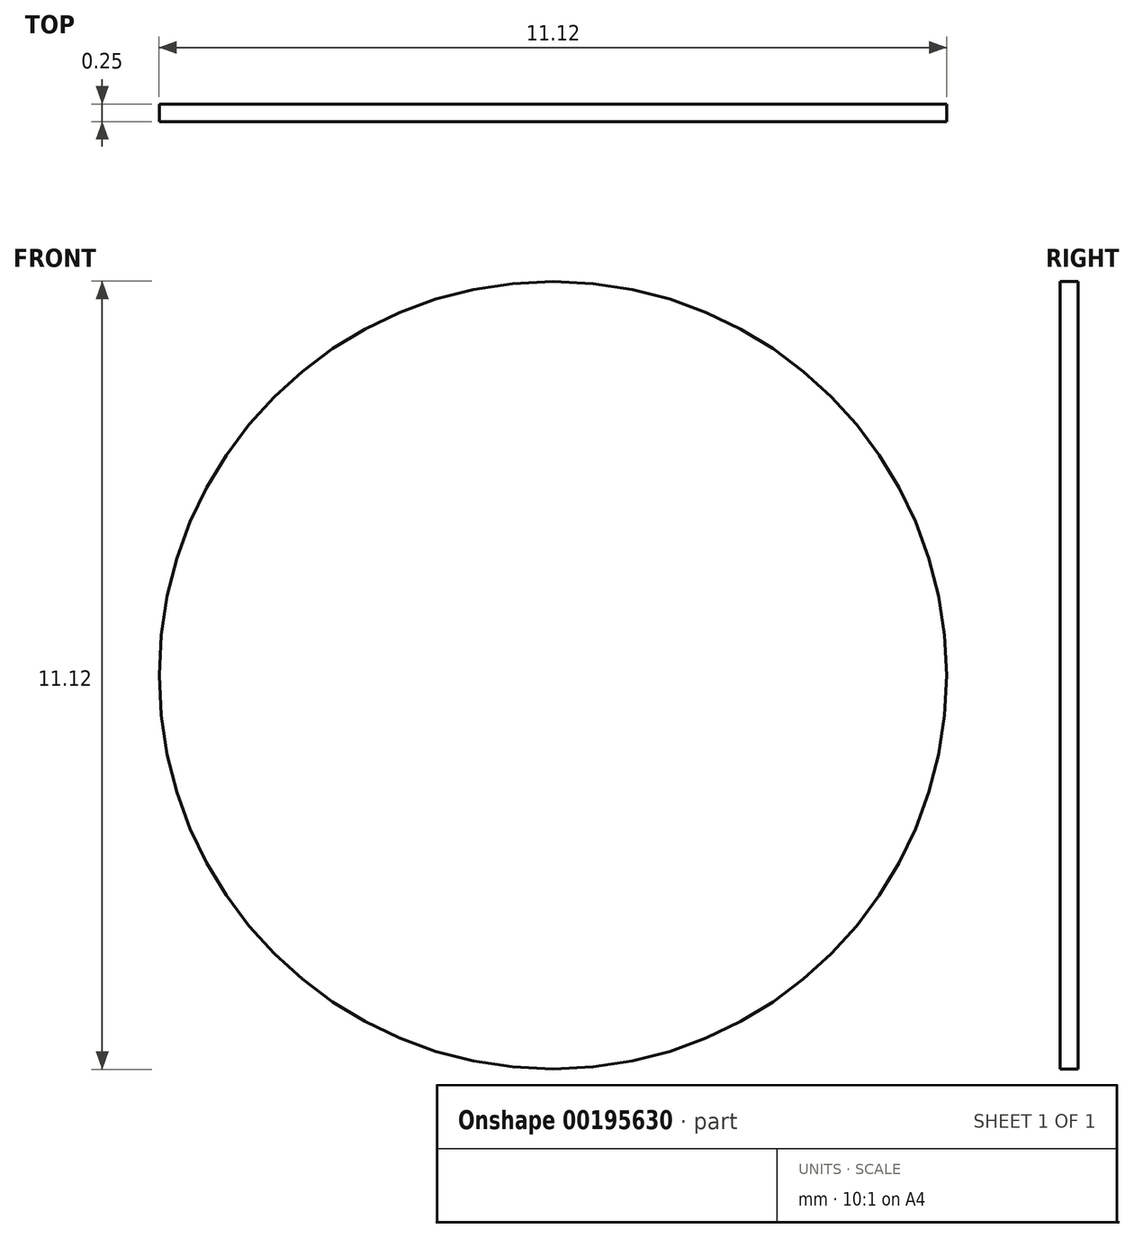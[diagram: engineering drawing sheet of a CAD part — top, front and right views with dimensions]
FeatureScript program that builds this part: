
annotation { "Feature Type Name" : "Feature", "Feature Type Description" : "" }
export const myFeature = defineFeature(function(context is Context, id is Id, definition is map)
    precondition{}
    {
        {
            var Q0;
            Q0=qCreatedBy(makeId("Front.planeOp"),FACE);
            var sketch = newSketch(context, id + "F0", { "sketchPlane" : qUnion([Q0])});
            skCircle(sketch, "E0", {"center": v(0, 0) * mm, "radius": 5.56 * mm});
            skSolve(sketch);
        }
        {
            var Q0;
            Q0 = qSketchRegion(id + "F0", true);
            extrude(context, id + "F1", {"entities" : qUnion([Q0]), "depth" : 0.25 * mm});
        }
    });
